# Revit family: Lockin Lockers AU_Seats_R22
name_source: partatom
category: Furniture
units: mm (PartAtom-declared; Revit-internal decimal feet)

## family parameters
Always vertical = Yes
Cut with Voids When Loaded = No
OmniClass Number = 23.40.20.27
OmniClass Title = Storage Shelving
Render Appearance Source = Family Geometry
Room Calculation Point = No
Shared = Yes
Work Plane-Based = Yes

## types (9) — shared parameters
Body/Frame Material = Material - Welded Steel - Oven-Baked Powdercoat
Desired Height = 450 mm  [stored 1.47638 ft]
Height Control = 450 mm  [stored 1.47638 ft]
Manufacturer = Lockin Lockers AU
Maximum Height = 450 mm  [stored 1.47638 ft]
Minimum Height = 450 mm  [stored 1.47638 ft]
Seat Material = Wood
URL = https://www.lockin.com.au
zero-valued in all types: Default Elevation

## per-type parameters (varying)
| type | Depth Control | Description | Desired Depth | Desired Width | Maximum Depth | Maximum Width | Minimum Depth | Minimum Width | Model | S1 | S2 | SOT | SS1 | SS2 | Seat Type | Width Control |
| Bench Seat Single (S1) | 490 mm  [stored 1.60761 ft] | Bench Seat Single | 490 mm  [stored 1.60761 ft] | 1500 mm  [stored 4.92126 ft] | 490 mm  [stored 1.60761 ft] | 2750 mm  [stored 9.02231 ft] | 490 mm  [stored 1.60761 ft] | 500 mm  [stored 1.64042 ft] | S1 | Yes | No | No | No | No | Lockin Lockers AU_Bench Seats_R22 : Bench Seat Single (S1) | 1500 mm  [stored 4.92126 ft] |
| Bench Seat Double (S2) | 890 mm  [stored 2.91995 ft] | Bench Seat Double | 890 mm  [stored 2.91995 ft] | 1500 mm  [stored 4.92126 ft] | 890 mm  [stored 2.91995 ft] | 2750 mm  [stored 9.02231 ft] | 890 mm  [stored 2.91995 ft] | 500 mm  [stored 1.64042 ft] | S2 | No | Yes | No | No | No | Lockin Lockers AU_Bench Seats_R22 : Bench Seat Double (S2) | 1500 mm  [stored 4.92126 ft] |
| Bench Seat double w. rail (SR) | 890 mm  [stored 2.91995 ft] | Bench Seat double w. rail | 890 mm  [stored 2.91995 ft] | 1500 mm  [stored 4.92126 ft] | 890 mm  [stored 2.91995 ft] | 2750 mm  [stored 9.02231 ft] | 890 mm  [stored 2.91995 ft] | 500 mm  [stored 1.64042 ft] | SR | No | Yes | No | No | No | Lockin Lockers AU_Bench Seats_R22 : Bench Seat double w. rail (SR) | 1500 mm  [stored 4.92126 ft] |
| Bench Seat Accessible double (ALS2) | 890 mm  [stored 2.91995 ft] | Bench Seat Accessible double | 890 mm  [stored 2.91995 ft] | 1500 mm  [stored 4.92126 ft] | 890 mm  [stored 2.91995 ft] | 2750 mm  [stored 9.02231 ft] | 890 mm  [stored 2.91995 ft] | 500 mm  [stored 1.64042 ft] | ALS2 | No | Yes | No | No | No | Lockin Lockers AU_Bench Seats_R22 : Bench Seat Accessible double (ALS2) | 1500 mm  [stored 4.92126 ft] |
| Bench Seat Accessible double w. rail (ALSR) | 890 mm  [stored 2.91995 ft] | Bench Seat Accessible double w. rail | 890 mm  [stored 2.91995 ft] | 1500 mm  [stored 4.92126 ft] | 890 mm  [stored 2.91995 ft] | 2750 mm  [stored 9.02231 ft] | 890 mm  [stored 2.91995 ft] | 500 mm  [stored 1.64042 ft] | ALSR | No | Yes | No | No | No | Lockin Lockers AU_Bench Seats_R22 : Bench Seat Accessible double w. rail (ALSR) | 1500 mm  [stored 4.92126 ft] |
| Shoe Seat Single (SS1) | 490 mm  [stored 1.60761 ft] | Shoe Seat Single | 490 mm  [stored 1.60761 ft] | 1500 mm  [stored 4.92126 ft] | 490 mm  [stored 1.60761 ft] | 2750 mm  [stored 9.02231 ft] | 490 mm  [stored 1.60761 ft] | 500 mm  [stored 1.64042 ft] | SS1 | No | No | No | Yes | No | Lockin Lockers AU_Shoe Seat_R22 : Shoe seat Single (SS1) | 1500 mm  [stored 4.92126 ft] |
| Shoe Seat Double (SS2) | 790 mm  [stored 2.59186 ft] | Shoe Seat Double | 490 mm  [stored 1.60761 ft] | 1500 mm  [stored 4.92126 ft] | 790 mm  [stored 2.59186 ft] | 2750 mm  [stored 9.02231 ft] | 790 mm  [stored 2.59186 ft] | 500 mm  [stored 1.64042 ft] | SS2 | No | No | No | No | Yes | Lockin Lockers AU_Shoe Seat_R22 : Shoe seat Double (SS2) | 1500 mm  [stored 4.92126 ft] |
| Ottoman - Round (SOT) | 800 mm  [stored 2.62467 ft] | Ottoman - Round | 800 mm  [stored 2.62467 ft] | 1800 mm  [stored 5.90551 ft] | 800 mm  [stored 2.62467 ft] | 2500 mm  [stored 8.2021 ft] | 800 mm  [stored 2.62467 ft] | 1500 mm  [stored 4.92126 ft] | SOT | No | No | Yes | No | No | Lockin Lockers AU_Ottoman_R22 : Ottoman - Round (SOT) | 1800 mm  [stored 5.90551 ft] |
| Ottoman - Square (SOT) | 800 mm  [stored 2.62467 ft] | Ottoman - Square | 800 mm  [stored 2.62467 ft] | 1800 mm  [stored 5.90551 ft] | 800 mm  [stored 2.62467 ft] | 2500 mm  [stored 8.2021 ft] | 800 mm  [stored 2.62467 ft] | 1500 mm  [stored 4.92126 ft] | SOT | No | No | Yes | No | No | Lockin Lockers AU_Ottoman_R22 : Ottoman - Square (SOT) | 1800 mm  [stored 5.90551 ft] |

note: [stored X ft] marks values corroborated as IEEE doubles in the binary element streams (Revit-internal decimal feet)

## geometry (parser evidence)
native form markers: Sweep x7
no freeform markers — native parametric forms only
